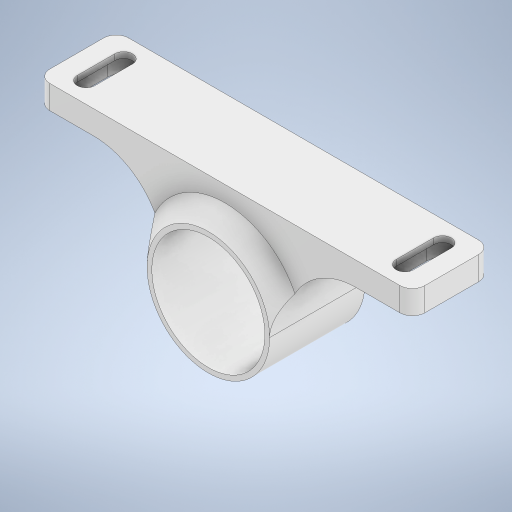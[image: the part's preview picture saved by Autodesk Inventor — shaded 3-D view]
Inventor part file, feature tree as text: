
AUTODESK INVENTOR PART (.ipt)
format: ipt  version: 2024.1 (Build 281209000, 209)  size: 528,896 bytes
history: native  units: in
note: dims shown in document units (in); Inventor stores cm internally (conversion verified against a paired STEP export)
features: extrude x5, sketch x5, fillet x1, chamfer x1, projected_geometry x1
ambient origin geometry x8: Origin, YZ Plane, XZ Plane, XY Plane, X Axis, Y Axis, Z Axis, Center Point
bodies: Solid1 (feature_tree)
feature tree (13):
  extrude  "Base"  Depth=3.75in
  extrude  "Extrusion2"  Depth=0.9371in
  extrude  "Bearing hole"  Depth=0.1657in TaperAngle=0.0deg
  extrude  "Slot"  Depth=0.375in
  extrude  "Counterbore"  Depth=0.125in
  fillet  "Fillet1"  Radius=0.1772in
  chamfer  "Chamfer2"  Distance=3.75in
  sketch  "Sketch1"  dims[d0=1.225in d4=3.75in]
  sketch  "Sketch2"  dims[d5=0.2362in d6=0.9371in]
  sketch  "Sketch3"  dims[d7=0.7874in d8=0.0in d9=0.1657in d10=0.0in]
  sketch  "Sketch4"  dims[d12=0.1772in d13=0.375in]
  projected_geometry  "Projected Loop1"
  sketch  "Sketch7"  dims[d15=0.2051in d16=0.0in d17=0.315in d18=0.1772in d19=0.0in d20=3.75in d21=3.75in d29=1.13in d30=1.0in d31=0.0in d39=0.125in d43=0.1657in d44=0.165in d45=45.0deg d22=0.5in d23=0.0344in d24=0.5in d25=0.0344in d46=0.0in d47=0.0in d48=0.0in d49=0.0in]
